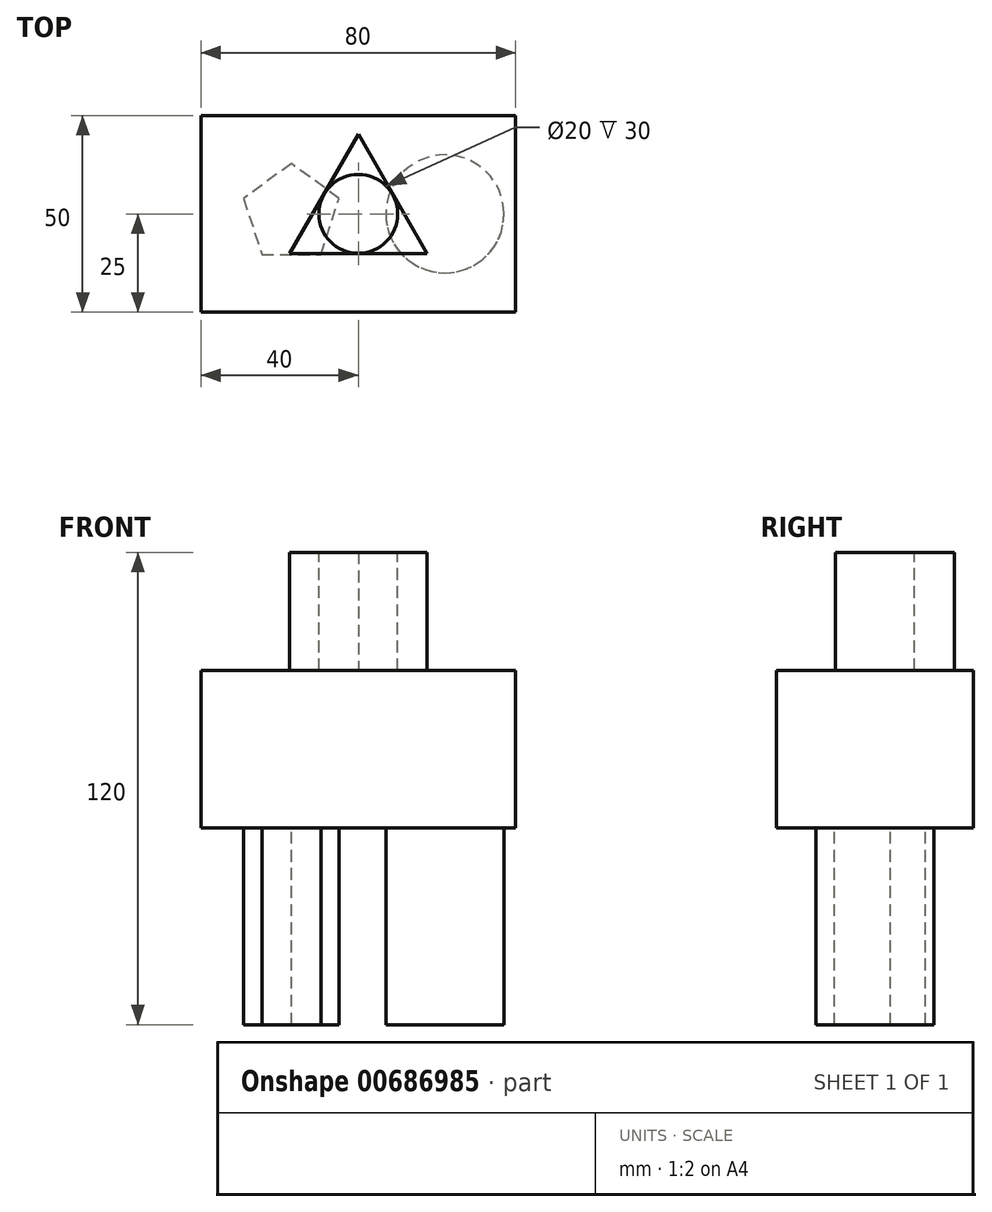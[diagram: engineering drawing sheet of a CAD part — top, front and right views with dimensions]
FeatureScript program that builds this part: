
annotation { "Feature Type Name" : "Feature", "Feature Type Description" : "" }
export const myFeature = defineFeature(function(context is Context, id is Id, definition is map)
    precondition{}
    {
        {
            var Q0;
            Q0=qCreatedBy(makeId("Top.planeOp"),FACE);
            var sketch = newSketch(context, id + "F0", { "sketchPlane" : qUnion([Q0])});
            skLineSegment(sketch, "E0.bottom", {"start": v(-40, 25) * mm, "end": v(40, 25) * mm});
            skLineSegment(sketch, "E0.top", {"start": v(-40, -25) * mm, "end": v(40, -25) * mm});
            skLineSegment(sketch, "E0.left", {"start": v(-40, 25) * mm, "end": v(-40, -25) * mm});
            skLineSegment(sketch, "E0.right", {"start": v(40, 25) * mm, "end": v(40, -25) * mm});
            skPoint(sketch, "E0.middle", {"position": v(0, 0) * mm});
            skSolve(sketch);
        }
        {
            var Q0;
            Q0 = qSketchRegion(id + "F0", true);
            extrude(context, id + "F1", {"entities" : qUnion([Q0]), "depth" : 40 * mm, "offsetDistance" : 25 * mm});
        }
        {
            var Q0;
            Q0=makeQuery(id+"F1.opExtrude","CAP_FACE",FACE,{"disambiguationData":[OSD([sQuery(id+"F0.wireOp",EDGE,"E0.bottom"),sQuery(id+"F0.wireOp",EDGE,"E0.top"),sQuery(id+"F0.wireOp",EDGE,"E0.left"),sQuery(id+"F0.wireOp",EDGE,"E0.right")])],"isStart":false});
            var sketch = newSketch(context, id + "F2", { "sketchPlane" : qUnion([Q0])});
            skCircle(sketch, "E1.cCircle", {"center": v(0, 0) * mm, "radius": 10.1 * mm, "construction": true});
            skLineSegment(sketch, "E1.0", {"start": v(-17.5, -10.1) * mm, "end": v(0, 20.2) * mm});
            skLineSegment(sketch, "E1.1", {"start": v(0, 20.2) * mm, "end": v(17.5, -10.1) * mm});
            skLineSegment(sketch, "E1.2", {"start": v(17.5, -10.1) * mm, "end": v(-17.5, -10.1) * mm});
            skPoint(sketch, "E1.0.midPoint", {"position": v(-8.75, 5.05) * mm});
            skSolve(sketch);
        }
        {
            var Q0;
            Q0 = qSketchRegion(id + "F2", true);
            extrude(context, id + "F3", {"entities" : qUnion([Q0]), "operationType" : NewBodyOperationType.ADD, "depth" : 30 * mm, "offsetDistance" : 25 * mm});
        }
        {
            var Q0;
            Q0=makeQuery(id+"F3.opExtrude","CAP_FACE",FACE,{"disambiguationData":[OSD([sQuery(id+"F2.wireOp",EDGE,"E1.0"),sQuery(id+"F2.wireOp",EDGE,"E1.1"),sQuery(id+"F2.wireOp",EDGE,"E1.2")])],"isStart":false});
            var sketch = newSketch(context, id + "F4", { "sketchPlane" : qUnion([Q0])});
            skCircle(sketch, "E2", {"center": v(0, 0) * mm, "radius": 10 * mm});
            skSolve(sketch);
        }
        {
            var Q0;
            Q0 = qSketchRegion(id + "F4", true);
            extrude(context, id + "F5", {"entities" : qUnion([Q0]), "operationType" : NewBodyOperationType.REMOVE, "oppositeDirection" : true, "depth" : 30 * mm, "offsetDistance" : 25 * mm});
        }
        {
            var Q0;
            Q0=makeQuery(id+"F1.opExtrude","CAP_FACE",FACE,{"disambiguationData":[OSD([sQuery(id+"F0.wireOp",EDGE,"E0.bottom"),sQuery(id+"F0.wireOp",EDGE,"E0.top"),sQuery(id+"F0.wireOp",EDGE,"E0.left"),sQuery(id+"F0.wireOp",EDGE,"E0.right")])],"isStart":true});
            var sketch = newSketch(context, id + "F6", { "sketchPlane" : qUnion([Q0])});
            skCircle(sketch, "E3.cCircle", {"center": v(-17, 0) * mm, "radius": 10.32 * mm, "construction": true});
            skLineSegment(sketch, "E3.0", {"start": v(-24.5, 10.32) * mm, "end": v(-9.5, 10.32) * mm});
            skLineSegment(sketch, "E3.1", {"start": v(-9.5, 10.32) * mm, "end": v(-4.86, -3.94) * mm});
            skLineSegment(sketch, "E3.2", {"start": v(-4.86, -3.94) * mm, "end": v(-17, -12.76) * mm});
            skLineSegment(sketch, "E3.3", {"start": v(-17, -12.76) * mm, "end": v(-29.14, -3.94) * mm});
            skLineSegment(sketch, "E3.4", {"start": v(-29.14, -3.94) * mm, "end": v(-24.5, 10.32) * mm});
            skPoint(sketch, "E3.0.midPoint", {"position": v(-17, 10.32) * mm});
            skSolve(sketch);
        }
        {
            var Q0;
            Q0 = qSketchRegion(id + "F6", true);
            extrude(context, id + "F7", {"entities" : qUnion([Q0]), "operationType" : NewBodyOperationType.ADD, "depth" : 50 * mm, "offsetDistance" : 25 * mm});
        }
        {
            var Q0;
            Q0=makeQuery(id+"F1.opExtrude","CAP_FACE",FACE,{"disambiguationData":[OSD([sQuery(id+"F0.wireOp",EDGE,"E0.bottom"),sQuery(id+"F0.wireOp",EDGE,"E0.top"),sQuery(id+"F0.wireOp",EDGE,"E0.left"),sQuery(id+"F0.wireOp",EDGE,"E0.right")])],"isStart":true});
            var sketch = newSketch(context, id + "F8", { "sketchPlane" : qUnion([Q0])});
            skCircle(sketch, "E4", {"center": v(22, 0) * mm, "radius": 15 * mm});
            skSolve(sketch);
        }
        {
            var Q0;
            Q0 = qSketchRegion(id + "F8", true);
            extrude(context, id + "F9", {"entities" : qUnion([Q0]), "operationType" : NewBodyOperationType.ADD, "depth" : 50 * mm, "offsetDistance" : 25 * mm});
        }
    });
